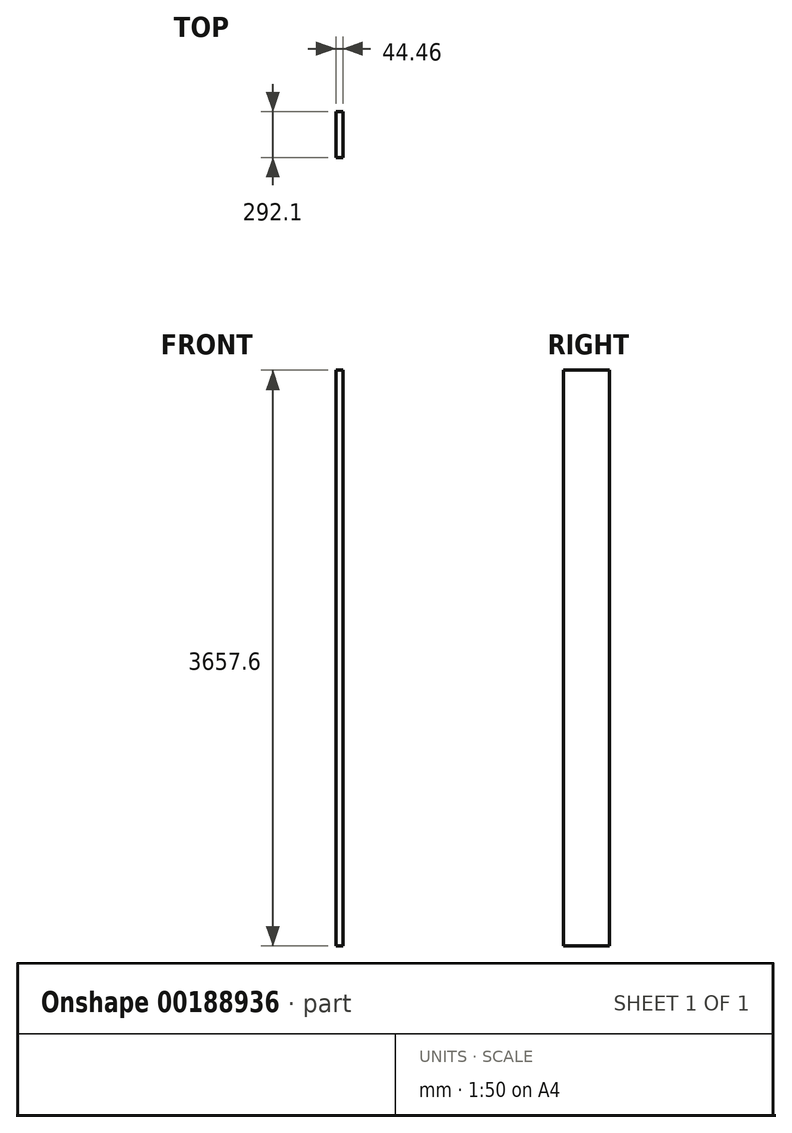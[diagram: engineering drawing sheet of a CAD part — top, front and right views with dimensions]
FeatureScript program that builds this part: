
annotation { "Feature Type Name" : "Feature", "Feature Type Description" : "" }
export const myFeature = defineFeature(function(context is Context, id is Id, definition is map)
    precondition{}
    {
        {
            var Q0;
            Q0=qCreatedBy(makeId("Top.planeOp"),FACE);
            var sketch = newSketch(context, id + "F1", { "sketchPlane" : qUnion([Q0])});
            skLineSegment(sketch, "E0.bottom", {"start": v(22.23, -146.05) * mm, "end": v(-22.22, -146.05) * mm});
            skLineSegment(sketch, "E0.top", {"start": v(22.23, 146.05) * mm, "end": v(-22.22, 146.05) * mm});
            skLineSegment(sketch, "E0.left", {"start": v(22.23, -146.05) * mm, "end": v(22.23, 146.05) * mm});
            skLineSegment(sketch, "E0.right", {"start": v(-22.22, -146.05) * mm, "end": v(-22.22, 146.05) * mm});
            skPoint(sketch, "E0.middle", {"position": v(0, 0) * mm});
            skSolve(sketch);
        }
        {
            var Q0;
            Q0=makeQuery(id+"F1.imprint","IMPRINT",FACE,{"disambiguationData":[TD([[makeQuery(id+"F1.imprint","IMPRINT",EDGE,{"derivedFrom":sQuery(id+"F1.wireOp",EDGE,"E0.bottom")}),-1.0]])]});
            extrude(context, id + "F0", {"entities" : qUnion([Q0]), "endBound" : BoundingType.SYMMETRIC, "depth" : 3657.6 * mm});
        }
    });
